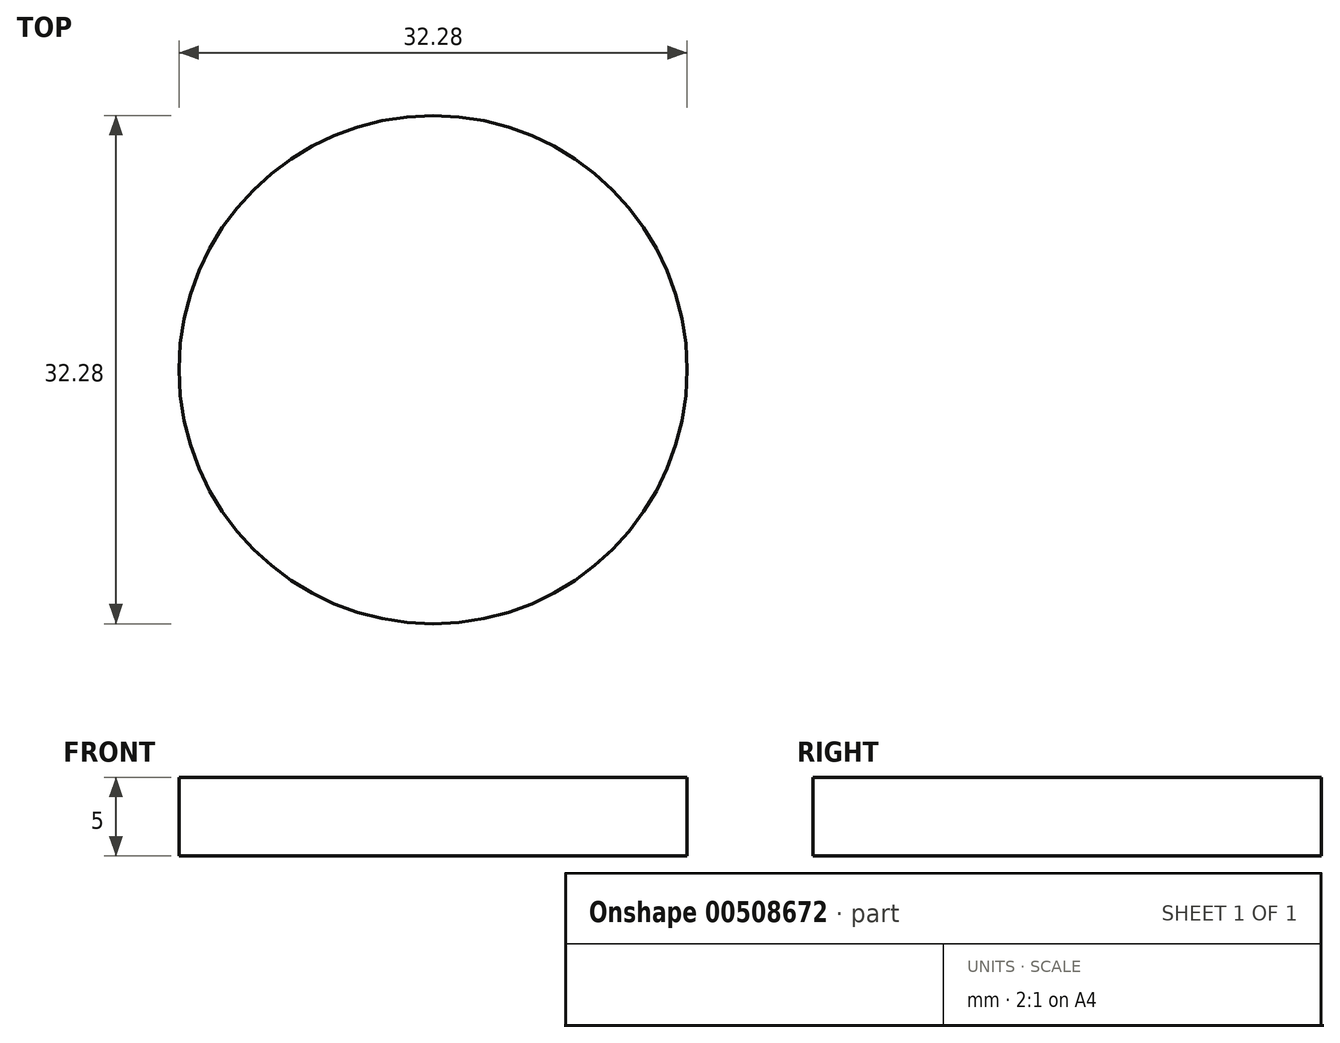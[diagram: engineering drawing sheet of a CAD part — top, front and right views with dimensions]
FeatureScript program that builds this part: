
annotation { "Feature Type Name" : "Feature", "Feature Type Description" : "" }
export const myFeature = defineFeature(function(context is Context, id is Id, definition is map)
    precondition{}
    {
        {
            var Q0;
            Q0=qCreatedBy(makeId("Top.planeOp"),FACE);
            var sketch = newSketch(context, id + "F0", { "sketchPlane" : qUnion([Q0])});
            skCircle(sketch, "E0", {"center": v(-17.33, 19.34) * mm, "radius": 16.14 * mm});
            skSolve(sketch);
        }
        {
            var Q0;
            Q0=makeQuery(id+"F0.imprint","IMPRINT",FACE,{"disambiguationData":[TD([[makeQuery(id+"F0.imprint","IMPRINT",EDGE,{"derivedFrom":sQuery(id+"F0.wireOp",EDGE,"E0")}),1.0]])]});
            extrude(context, id + "F1", {"entities" : qUnion([Q0]), "depth" : 5 * mm});
        }
    });
